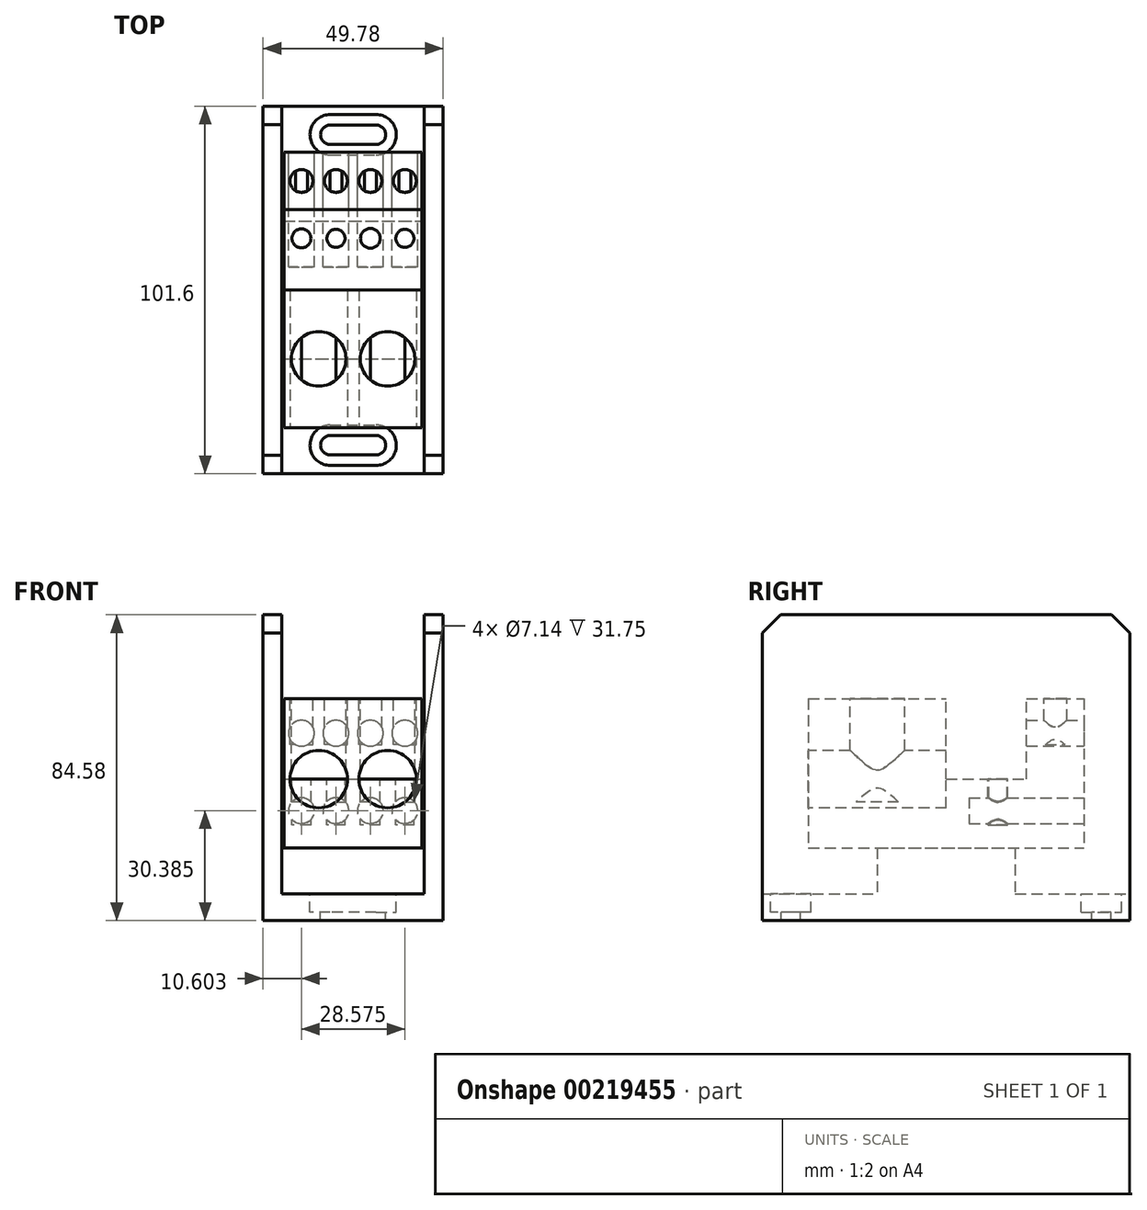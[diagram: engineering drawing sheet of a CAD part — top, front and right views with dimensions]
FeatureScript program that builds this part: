
annotation { "Feature Type Name" : "Feature", "Feature Type Description" : "" }
export const myFeature = defineFeature(function(context is Context, id is Id, definition is map)
    precondition{}
    {
        {
            var Q0;
            Q0=qCreatedBy(makeId("Top.planeOp"),FACE);
            var sketch = newSketch(context, id + "F0", { "sketchPlane" : qUnion([Q0])});
            skLineSegment(sketch, "E0.bottom", {"start": v(-24.9, -50.8) * mm, "end": v(24.9, -50.8) * mm});
            skLineSegment(sketch, "E0.top", {"start": v(-24.9, 50.8) * mm, "end": v(24.9, 50.8) * mm});
            skLineSegment(sketch, "E0.left", {"start": v(-24.9, -50.8) * mm, "end": v(-24.9, 50.8) * mm});
            skLineSegment(sketch, "E0.right", {"start": v(24.9, -50.8) * mm, "end": v(24.9, 50.8) * mm});
            skPoint(sketch, "E0.middle", {"position": v(0, 0) * mm});
            skSolve(sketch);
        }
        {
            var Q0;
            Q0=qSketchRegion(id+"F0",true);
            extrude(context, id + "F1", {"entities" : qUnion([Q0]), "depth" : 84.58 * mm});
        }
        {
            var Q0;
            Q0=makeQuery(id+"F1.opExtrude","CAP_FACE",FACE,{"disambiguationData":[OSD([sQuery(id+"F0.wireOp",EDGE,"E0.bottom"),sQuery(id+"F0.wireOp",EDGE,"E0.top"),sQuery(id+"F0.wireOp",EDGE,"E0.left"),sQuery(id+"F0.wireOp",EDGE,"E0.right")])],"isStart":false});
            var sketch = newSketch(context, id + "F2", { "sketchPlane" : qUnion([Q0])});
            skLineSegment(sketch, "E1.bottom", {"start": v(19.69, -50.8) * mm, "end": v(-19.69, -50.8) * mm});
            skLineSegment(sketch, "E1.top", {"start": v(19.69, 50.8) * mm, "end": v(-19.69, 50.8) * mm});
            skLineSegment(sketch, "E1.left", {"start": v(19.69, -50.8) * mm, "end": v(19.69, 50.8) * mm});
            skLineSegment(sketch, "E1.right", {"start": v(-19.69, -50.8) * mm, "end": v(-19.69, 50.8) * mm});
            skPoint(sketch, "E1.middle", {"position": v(0, 0) * mm});
            skSolve(sketch);
        }
        {
            var Q0;
            Q0=qSketchRegion(id+"F2",true);
            extrude(context, id + "F3", {"entities" : qUnion([Q0]), "operationType" : NewBodyOperationType.REMOVE, "oppositeDirection" : true, "depth" : 77.22 * mm});
        }
        {
            var Q0;
            Q0=makeQuery(id+"F3.boolean.opBoolean","COPY",FACE,{"derivedFrom":makeQuery(id+"F3.opExtrude","CAP_FACE",FACE,{"disambiguationData":[OSD([sQuery(id+"F2.wireOp",EDGE,"E1.bottom"),sQuery(id+"F2.wireOp",EDGE,"E1.top"),sQuery(id+"F2.wireOp",EDGE,"E1.left"),sQuery(id+"F2.wireOp",EDGE,"E1.right")])],"isStart":false})});
            var sketch = newSketch(context, id + "F4", { "sketchPlane" : qUnion([Q0])});
            skLineSegment(sketch, "E2.bottom", {"start": v(6.35, 40.26) * mm, "end": v(-6.35, 40.26) * mm});
            skLineSegment(sketch, "E2.top", {"start": v(6.35, 45.6) * mm, "end": v(-6.35, 45.6) * mm});
            skLineSegment(sketch, "E2.left", {"start": v(6.35, 40.26) * mm, "end": v(6.35, 45.6) * mm});
            skLineSegment(sketch, "E2.right", {"start": v(-6.35, 40.26) * mm, "end": v(-6.35, 45.6) * mm});
            skPoint(sketch, "E2.middle", {"position": v(0, 42.93) * mm});
            skLineSegment(sketch, "E3.bottom", {"start": v(-6.35, -40.26) * mm, "end": v(6.35, -40.26) * mm});
            skLineSegment(sketch, "E3.top", {"start": v(-6.35, -45.6) * mm, "end": v(6.35, -45.6) * mm});
            skLineSegment(sketch, "E3.left", {"start": v(-6.35, -40.26) * mm, "end": v(-6.35, -45.6) * mm});
            skLineSegment(sketch, "E3.right", {"start": v(6.35, -40.26) * mm, "end": v(6.35, -45.6) * mm});
            skPoint(sketch, "E3.middle", {"position": v(0, -42.93) * mm});
            skArc(sketch, "E4", {"start": v(-6.35, 45.6) * mm, "mid": v(-9.02, 42.93) * mm, "end": v(-6.35, 40.26) * mm});
            skArc(sketch, "E5", {"start": v(6.35, 40.26) * mm, "mid": v(9.02, 42.93) * mm, "end": v(6.35, 45.6) * mm});
            skArc(sketch, "E6", {"start": v(-6.35, -40.26) * mm, "mid": v(-9.02, -42.93) * mm, "end": v(-6.35, -45.6) * mm});
            skArc(sketch, "E7", {"start": v(6.35, -45.6) * mm, "mid": v(9.02, -42.93) * mm, "end": v(6.35, -40.26) * mm});
            skSolve(sketch);
        }
        {
            var Q0;
            Q0=qSketchRegion(id+"F4",true);
            extrude(context, id + "F5", {"entities" : qUnion([Q0]), "operationType" : NewBodyOperationType.REMOVE, "oppositeDirection" : true, "depth" : 7.37 * mm});
        }
        {
            var Q0;
            {var subQ0=sQuery(id+"F0.wireOp",EDGE,"E0.left");var subQ1=sQuery(id+"F0.wireOp",EDGE,"E0.top");Q0=makeQuery(id+"F3.boolean.opBoolean","SPLIT",EDGE,{"disambiguationData":[TD([makeQuery(id+"F1.opExtrude","SWEPT_FACE",FACE,{"disambiguationData":[OSD([subQ0])]})])],"derivedFrom":makeQuery(id+"F1.opExtrude","CAP_EDGE",EDGE,{"disambiguationData":[OSD([subQ1])],"isStart":false})});}
            var Q1;
            {var subQ0=sQuery(id+"F0.wireOp",EDGE,"E0.right");var subQ1=sQuery(id+"F0.wireOp",EDGE,"E0.top");Q1=makeQuery(id+"F3.boolean.opBoolean","SPLIT",EDGE,{"disambiguationData":[TD([makeQuery(id+"F1.opExtrude","SWEPT_FACE",FACE,{"disambiguationData":[OSD([subQ0])]})])],"derivedFrom":makeQuery(id+"F1.opExtrude","CAP_EDGE",EDGE,{"disambiguationData":[OSD([subQ1])],"isStart":false})});}
            var Q2;
            {var subQ0=sQuery(id+"F0.wireOp",EDGE,"E0.bottom");var subQ1=sQuery(id+"F0.wireOp",EDGE,"E0.left");Q2=makeQuery(id+"F3.boolean.opBoolean","SPLIT",EDGE,{"disambiguationData":[TD([makeQuery(id+"F1.opExtrude","SWEPT_FACE",FACE,{"disambiguationData":[OSD([subQ1])]})])],"derivedFrom":makeQuery(id+"F1.opExtrude","CAP_EDGE",EDGE,{"disambiguationData":[OSD([subQ0])],"isStart":false})});}
            var Q3;
            {var subQ0=sQuery(id+"F0.wireOp",EDGE,"E0.bottom");var subQ1=sQuery(id+"F0.wireOp",EDGE,"E0.right");Q3=makeQuery(id+"F3.boolean.opBoolean","SPLIT",EDGE,{"disambiguationData":[TD([makeQuery(id+"F1.opExtrude","SWEPT_FACE",FACE,{"disambiguationData":[OSD([subQ1])]})])],"derivedFrom":makeQuery(id+"F1.opExtrude","CAP_EDGE",EDGE,{"disambiguationData":[OSD([subQ0])],"isStart":false})});}
            chamfer(context, id + "F6", {"entities" : qUnion([Q0, Q1, Q2, Q3]), "width" : 5.08 * mm, "tangentPropagation" : true});
        }
        {
            var Q0;
            Q0=makeQuery(id+"F3.boolean.opBoolean","COPY",FACE,{"derivedFrom":makeQuery(id+"F3.opExtrude","CAP_FACE",FACE,{"disambiguationData":[OSD([sQuery(id+"F2.wireOp",EDGE,"E1.bottom"),sQuery(id+"F2.wireOp",EDGE,"E1.top"),sQuery(id+"F2.wireOp",EDGE,"E1.left"),sQuery(id+"F2.wireOp",EDGE,"E1.right")])],"isStart":false})});
            var sketch = newSketch(context, id + "F7", { "sketchPlane" : qUnion([Q0])});
            skLineSegment(sketch, "E8.bottom", {"start": v(-6.35, 37.34) * mm, "end": v(6.35, 37.34) * mm});
            skLineSegment(sketch, "E8.top", {"start": v(-6.35, 48.51) * mm, "end": v(6.35, 48.51) * mm});
            skLineSegment(sketch, "E8.left", {"start": v(-6.35, 37.34) * mm, "end": v(-6.35, 48.51) * mm});
            skLineSegment(sketch, "E8.right", {"start": v(6.35, 37.34) * mm, "end": v(6.35, 48.51) * mm});
            skPoint(sketch, "E8.middle", {"position": v(0, 42.93) * mm});
            skLineSegment(sketch, "E9.bottom", {"start": v(-6.35, -48.51) * mm, "end": v(6.35, -48.51) * mm});
            skLineSegment(sketch, "E9.top", {"start": v(-6.35, -37.34) * mm, "end": v(6.35, -37.34) * mm});
            skLineSegment(sketch, "E9.left", {"start": v(-6.35, -48.51) * mm, "end": v(-6.35, -37.34) * mm});
            skLineSegment(sketch, "E9.right", {"start": v(6.35, -48.51) * mm, "end": v(6.35, -37.34) * mm});
            skPoint(sketch, "E9.middle", {"position": v(0, -42.93) * mm});
            skArc(sketch, "E10", {"start": v(-6.35, 48.51) * mm, "mid": v(-11.94, 42.93) * mm, "end": v(-6.35, 37.34) * mm});
            skArc(sketch, "E11", {"start": v(6.35, 37.34) * mm, "mid": v(11.94, 42.93) * mm, "end": v(6.35, 48.51) * mm});
            skArc(sketch, "E12", {"start": v(-6.35, -37.34) * mm, "mid": v(-11.94, -42.93) * mm, "end": v(-6.35, -48.51) * mm});
            skArc(sketch, "E13", {"start": v(6.35, -48.51) * mm, "mid": v(11.94, -42.93) * mm, "end": v(6.35, -37.34) * mm});
            skSolve(sketch);
        }
        {
            var Q0;
            Q0=qSketchRegion(id+"F7",true);
            extrude(context, id + "F8", {"entities" : qUnion([Q0]), "operationType" : NewBodyOperationType.REMOVE, "oppositeDirection" : true, "depth" : 5.08 * mm});
        }
        {
            var Q0;
            Q0=makeQuery(id+"F3.boolean.opBoolean","COPY",FACE,{"derivedFrom":makeQuery(id+"F3.opExtrude","CAP_FACE",FACE,{"disambiguationData":[OSD([sQuery(id+"F2.wireOp",EDGE,"E1.bottom"),sQuery(id+"F2.wireOp",EDGE,"E1.top"),sQuery(id+"F2.wireOp",EDGE,"E1.left"),sQuery(id+"F2.wireOp",EDGE,"E1.right")])],"isStart":false})});
            var sketch = newSketch(context, id + "F9", { "sketchPlane" : qUnion([Q0])});
            skLineSegment(sketch, "E14.bottom", {"start": v(-19.69, -19.05) * mm, "end": v(19.69, -19.05) * mm});
            skLineSegment(sketch, "E14.top", {"start": v(-19.69, 19.05) * mm, "end": v(19.69, 19.05) * mm});
            skLineSegment(sketch, "E14.left", {"start": v(-19.69, -19.05) * mm, "end": v(-19.69, 19.05) * mm});
            skLineSegment(sketch, "E14.right", {"start": v(19.69, -19.05) * mm, "end": v(19.69, 19.05) * mm});
            skPoint(sketch, "E14.middle", {"position": v(0, 0) * mm});
            skSolve(sketch);
        }
        {
            var Q0;
            Q0=qSketchRegion(id+"F9",true);
            extrude(context, id + "F10", {"entities" : qUnion([Q0]), "operationType" : NewBodyOperationType.ADD, "depth" : 12.7 * mm});
        }
        {
            var Q0;
            Q0=makeQuery(id+"F10.opExtrude","CAP_FACE",FACE,{"disambiguationData":[OSD([sQuery(id+"F9.wireOp",EDGE,"E14.bottom"),sQuery(id+"F9.wireOp",EDGE,"E14.top"),sQuery(id+"F9.wireOp",EDGE,"E14.left"),sQuery(id+"F9.wireOp",EDGE,"E14.right")])],"isStart":false});
            var sketch = newSketch(context, id + "F11", { "sketchPlane" : qUnion([Q0])});
            skLineSegment(sketch, "E15.bottom", {"start": v(-19.05, -38.1) * mm, "end": v(19.05, -38.1) * mm});
            skLineSegment(sketch, "E15.top", {"start": v(-19.05, 38.1) * mm, "end": v(19.05, 38.1) * mm});
            skLineSegment(sketch, "E15.left", {"start": v(-19.05, -38.1) * mm, "end": v(-19.05, 38.1) * mm});
            skLineSegment(sketch, "E15.right", {"start": v(19.05, -38.1) * mm, "end": v(19.05, 38.1) * mm});
            skPoint(sketch, "E15.middle", {"position": v(0, 0) * mm});
            skSolve(sketch);
        }
        {
            var Q0;
            Q0=qSketchRegion(id+"F11",true);
            extrude(context, id + "F12", {"entities" : qUnion([Q0]), "depth" : 41.27 * mm});
        }
        {
            var Q0;
            Q0=makeQuery(id+"F12.opExtrude","CAP_FACE",FACE,{"disambiguationData":[OSD([sQuery(id+"F11.wireOp",EDGE,"E15.bottom"),sQuery(id+"F11.wireOp",EDGE,"E15.top"),sQuery(id+"F11.wireOp",EDGE,"E15.left"),sQuery(id+"F11.wireOp",EDGE,"E15.right")])],"isStart":false});
            var sketch = newSketch(context, id + "F13", { "sketchPlane" : qUnion([Q0])});
            skLineSegment(sketch, "E16.bottom", {"start": v(-19.05, 0) * mm, "end": v(19.05, 0) * mm});
            skLineSegment(sketch, "E16.top", {"start": v(-19.05, 22.23) * mm, "end": v(19.05, 22.23) * mm});
            skLineSegment(sketch, "E16.left", {"start": v(-19.05, 0) * mm, "end": v(-19.05, 22.23) * mm});
            skLineSegment(sketch, "E16.right", {"start": v(19.05, 0) * mm, "end": v(19.05, 22.23) * mm});
            skSolve(sketch);
        }
        {
            var Q0;
            Q0=qSketchRegion(id+"F13",true);
            extrude(context, id + "F14", {"entities" : qUnion([Q0]), "operationType" : NewBodyOperationType.REMOVE, "oppositeDirection" : true, "depth" : 22.22 * mm});
        }
        {
            var Q0;
            {var subQ0=sQuery(id+"F11.wireOp",EDGE,"E15.bottom");var subQ1=sQuery(id+"F11.wireOp",EDGE,"E15.left");var subQ2=sQuery(id+"F11.wireOp",EDGE,"E15.right");Q0=makeQuery(id+"F14.boolean.opBoolean","SPLIT",FACE,{"disambiguationData":[TD([makeQuery(id+"F12.opExtrude","SWEPT_FACE",FACE,{"disambiguationData":[OSD([subQ0])]})])],"derivedFrom":makeQuery(id+"F12.opExtrude","CAP_FACE",FACE,{"disambiguationData":[OSD([subQ0,sQuery(id+"F11.wireOp",EDGE,"E15.top"),subQ1,subQ2])],"isStart":false})});}
            var sketch = newSketch(context, id + "F15", { "sketchPlane" : qUnion([Q0])});
            skCircle(sketch, "E17", {"center": v(-9.53, -19.05) * mm, "radius": 7.54 * mm});
            skCircle(sketch, "E18", {"center": v(9.53, -19.05) * mm, "radius": 7.54 * mm});
            skSolve(sketch);
        }
        {
            var Q0;
            Q0=qSketchRegion(id+"F15",true);
            extrude(context, id + "F16", {"entities" : qUnion([Q0]), "operationType" : NewBodyOperationType.REMOVE, "oppositeDirection" : true, "depth" : 28.57 * mm});
        }
        {
            var Q0;
            Q0=makeQuery(id+"F12.opExtrude","SWEPT_FACE",FACE,{"disambiguationData":[OSD([sQuery(id+"F11.wireOp",EDGE,"E15.bottom")])]});
            var sketch = newSketch(context, id + "F17", { "sketchPlane" : qUnion([Q0])});
            skCircle(sketch, "E19", {"center": v(-9.52, 39.12) * mm, "radius": 7.94 * mm});
            skCircle(sketch, "E20", {"center": v(9.53, 39.12) * mm, "radius": 7.94 * mm});
            skSolve(sketch);
        }
        {
            var Q0;
            Q0=qSketchRegion(id+"F17",true);
            extrude(context, id + "F18", {"entities" : qUnion([Q0]), "operationType" : NewBodyOperationType.REMOVE, "oppositeDirection" : true, "depth" : 38.1 * mm});
        }
        {
            var Q0;
            {var subQ0=sQuery(id+"F11.wireOp",EDGE,"E15.top");var subQ1=sQuery(id+"F11.wireOp",EDGE,"E15.left");var subQ2=sQuery(id+"F11.wireOp",EDGE,"E15.right");Q0=makeQuery(id+"F14.boolean.opBoolean","SPLIT",FACE,{"disambiguationData":[TD([makeQuery(id+"F12.opExtrude","SWEPT_FACE",FACE,{"disambiguationData":[OSD([subQ0])]})])],"derivedFrom":makeQuery(id+"F12.opExtrude","CAP_FACE",FACE,{"disambiguationData":[OSD([sQuery(id+"F11.wireOp",EDGE,"E15.bottom"),subQ0,subQ1,subQ2])],"isStart":false})});}
            var sketch = newSketch(context, id + "F19", { "sketchPlane" : qUnion([Q0])});
            skCircle(sketch, "E21", {"center": v(-4.76, 30.16) * mm, "radius": 3.18 * mm});
            skCircle(sketch, "E22", {"center": v(4.76, 30.16) * mm, "radius": 3.18 * mm});
            skCircle(sketch, "E23", {"center": v(14.29, 30.16) * mm, "radius": 3.18 * mm});
            skCircle(sketch, "E24", {"center": v(-14.29, 30.16) * mm, "radius": 3.18 * mm});
            skSolve(sketch);
        }
        {
            var Q0;
            Q0=qSketchRegion(id+"F19",true);
            extrude(context, id + "F20", {"entities" : qUnion([Q0]), "operationType" : NewBodyOperationType.REMOVE, "oppositeDirection" : true, "depth" : 12.7 * mm});
        }
        {
            var Q0;
            Q0=makeQuery(id+"F14.boolean.opBoolean","COPY",FACE,{"derivedFrom":makeQuery(id+"F14.opExtrude","CAP_FACE",FACE,{"disambiguationData":[OSD([sQuery(id+"F13.wireOp",EDGE,"E16.bottom"),sQuery(id+"F13.wireOp",EDGE,"E16.top"),sQuery(id+"F13.wireOp",EDGE,"E16.left"),sQuery(id+"F13.wireOp",EDGE,"E16.right")])],"isStart":false})});
            var sketch = newSketch(context, id + "F21", { "sketchPlane" : qUnion([Q0])});
            skCircle(sketch, "E25", {"center": v(-4.76, 14.29) * mm, "radius": 2.52 * mm});
            skCircle(sketch, "E26", {"center": v(-14.29, 14.29) * mm, "radius": 2.62 * mm});
            skCircle(sketch, "E27", {"center": v(4.76, 14.29) * mm, "radius": 2.73 * mm});
            skCircle(sketch, "E28", {"center": v(14.29, 14.29) * mm, "radius": 2.52 * mm});
            skSolve(sketch);
        }
        {
            var Q0;
            Q0=qSketchRegion(id+"F21",true);
            extrude(context, id + "F22", {"entities" : qUnion([Q0]), "operationType" : NewBodyOperationType.REMOVE, "oppositeDirection" : true, "depth" : 12.7 * mm});
        }
        {
            var Q0;
            Q0=makeQuery(id+"F12.opExtrude","SWEPT_FACE",FACE,{"disambiguationData":[OSD([sQuery(id+"F11.wireOp",EDGE,"E15.top")])]});
            var sketch = newSketch(context, id + "F23", { "sketchPlane" : qUnion([Q0])});
            skCircle(sketch, "E29", {"center": v(-4.76, 51.82) * mm, "radius": 3.57 * mm});
            skCircle(sketch, "E30", {"center": v(-14.29, 51.82) * mm, "radius": 3.57 * mm});
            skCircle(sketch, "E31", {"center": v(4.76, 51.82) * mm, "radius": 3.57 * mm});
            skCircle(sketch, "E32", {"center": v(14.29, 51.82) * mm, "radius": 3.57 * mm});
            skCircle(sketch, "E33", {"center": v(-4.76, 30.38) * mm, "radius": 3.57 * mm});
            skCircle(sketch, "E34", {"center": v(-14.29, 30.38) * mm, "radius": 3.57 * mm});
            skCircle(sketch, "E35", {"center": v(4.76, 30.38) * mm, "radius": 3.57 * mm});
            skCircle(sketch, "E36", {"center": v(14.29, 30.38) * mm, "radius": 3.57 * mm});
            skSolve(sketch);
        }
        {
            var Q0;
            Q0=qSketchRegion(id+"F23",true);
            extrude(context, id + "F24", {"entities" : qUnion([Q0]), "operationType" : NewBodyOperationType.REMOVE, "oppositeDirection" : true, "depth" : 31.75 * mm});
        }
    });
